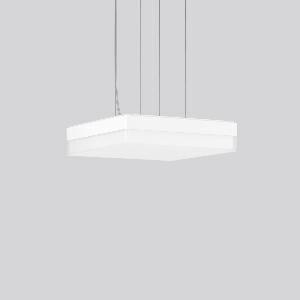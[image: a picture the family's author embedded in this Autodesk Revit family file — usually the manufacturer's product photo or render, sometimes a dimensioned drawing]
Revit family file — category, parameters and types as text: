
# Revit family: flat_slim_square_312541_002_76_8cef
name_source: partatom
category: Lighting Fixtures
units: mm (PartAtom-declared; Revit-internal decimal feet)

## family parameters
Cut with Voids When Loaded = No
Host = Face
Light Source = No
Part Type = Normal
Room Calculation Point = No
Round Connector Dimension = Use Diameter
Shared = No

## types (1)
- MultiLumen 2 840 (1 x LED Modul 840, 2400 lm, 4000)
    Apparent Load = 21 VA
    CIE Flux Codes = 43 74 93 92 100
    Color Rendering = 80
    Color Temperature = 4000
    Default Elevation = 1800 mm
    Height = 70 mm
    Lamp = 1 x LED Modul 840
    Lamp Light Flux = 2400 lm
    Lamp count = 1
    Length = 300 mm
    Lifetime = 50000 h
    Luminous efficacy = 114 lm/W
    Manufacturer = RZB
    ModVariant = No
    Model = 312541.002.76
    Mounting Place = Ceiling
    Mounting Type = Pendant
    Number of Poles = 1
    OnlyDefault = Yes
    Power Factor = 1
    Product Name = FLAT SLIM square
    Product group = Pendant luminaires
    ProductGroupID = 902
    Protection Class = Protection class I
    Protection Degree = IP 40
    RLX_Detail_Level = 1
    RLX_Emergency_Light_Flux = 0 lm
    RLX_Emergency_Type = 0
    RLX_Emergency_Type_DB = No
    RlxData = <blob elided: 14245 chars, md5=0daf02c5>
    Socket = socket
    Standby Power = 0 W
    System Light Flux = 2400 lm
    System Power = 21 W
    Type Comments = MultiLumen 2 840
    Type Image = 312541.002.jpg
    URL = http://relux.com
    VarID = multilumen_2_840
    Voltage = 230 V
    Voltage Range = 220-240 V
    Weight = 0.00 kg
    Width = 300 mm

## geometry (parser evidence)
native form markers: Sweep x13
no freeform markers — native parametric forms only
